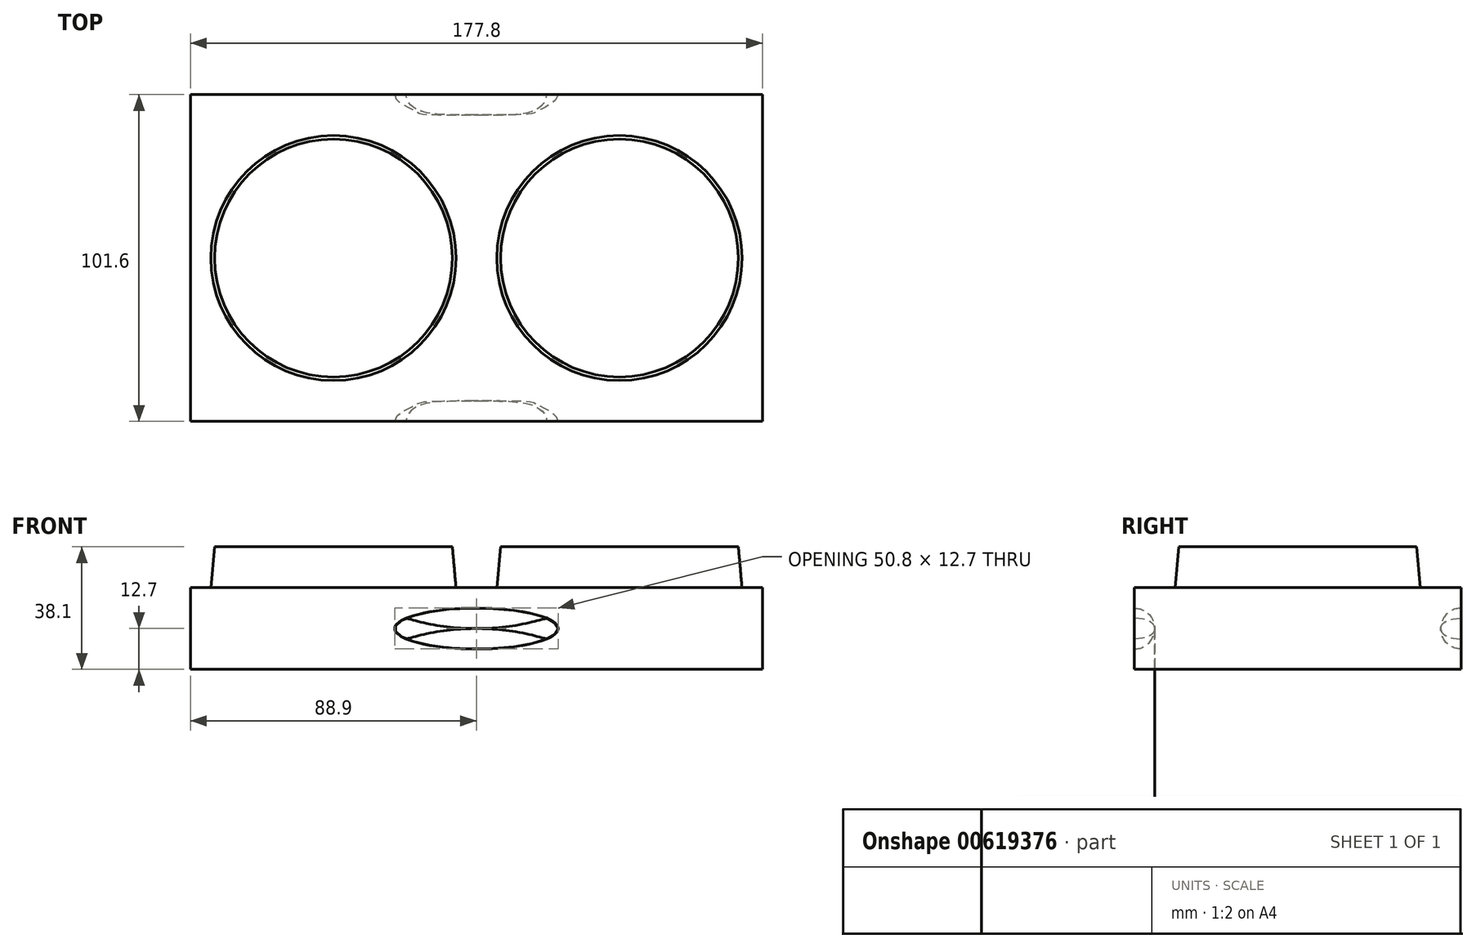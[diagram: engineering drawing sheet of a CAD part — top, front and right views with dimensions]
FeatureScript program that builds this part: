
annotation { "Feature Type Name" : "Feature", "Feature Type Description" : "" }
export const myFeature = defineFeature(function(context is Context, id is Id, definition is map)
    precondition{}
    {
        {
            var Q0;
            Q0=qCreatedBy(makeId("Top.planeOp"),FACE);
            var sketch = newSketch(context, id + "F0", { "sketchPlane" : qUnion([Q0])});
            skLineSegment(sketch, "E0.bottom", {"start": v(-88.9, 50.8) * mm, "end": v(88.9, 50.8) * mm});
            skLineSegment(sketch, "E0.top", {"start": v(-88.9, -50.8) * mm, "end": v(88.9, -50.8) * mm});
            skLineSegment(sketch, "E0.left", {"start": v(-88.9, 50.8) * mm, "end": v(-88.9, -50.8) * mm});
            skLineSegment(sketch, "E0.right", {"start": v(88.9, 50.8) * mm, "end": v(88.9, -50.8) * mm});
            skSolve(sketch);
        }
        {
            var Q0;
            Q0 = qSketchRegion(id + "F0", true);
            extrude(context, id + "F1", {"entities" : qUnion([Q0]), "depth" : 25.4 * mm, "offsetDistance" : 25.4 * mm});
        }
        {
            var Q0;
            Q0=makeQuery(id+"F1.opExtrude","CAP_FACE",FACE,{"disambiguationData":[OSD([sQuery(id+"F0.wireOp",EDGE,"E0.bottom"),sQuery(id+"F0.wireOp",EDGE,"E0.top"),sQuery(id+"F0.wireOp",EDGE,"E0.left"),sQuery(id+"F0.wireOp",EDGE,"E0.right")])],"isStart":false});
            var sketch = newSketch(context, id + "F2", { "sketchPlane" : qUnion([Q0])});
            skCircle(sketch, "E1", {"center": v(-44.45, 0) * mm, "radius": 38.09 * mm});
            skCircle(sketch, "E2", {"center": v(44.45, 0) * mm, "radius": 38.09 * mm});
            skSolve(sketch);
        }
        {
            var Q0;
            Q0 = qSketchRegion(id + "F2", true);
            extrude(context, id + "F3", {"entities" : qUnion([Q0]), "operationType" : NewBodyOperationType.ADD, "depth" : 12.7 * mm, "offsetDistance" : 25.4 * mm, "hasDraft" : true, "draftAngle" : 5 * degree, "draftPullDirection" : true});
        }
        {
            var Q0;
            Q0=makeQuery(id+"F1.opExtrude","SWEPT_FACE",FACE,{"disambiguationData":[OSD([sQuery(id+"F0.wireOp",EDGE,"E0.top")])]});
            var sketch = newSketch(context, id + "F4", { "sketchPlane" : qUnion([Q0])});
            skEllipse(sketch, "E3", {"center": v(0, 12.7) * mm, "majorRadius": 25.4 * mm, "minorRadius": 6.35 * mm, "majorAxis": v(1, 0)});
            skSolve(sketch);
        }
        {
            var Q0;
            Q0 = qSketchRegion(id + "F4", true);
            extrude(context, id + "F5", {"entities" : qUnion([Q0]), "operationType" : NewBodyOperationType.REMOVE, "oppositeDirection" : true, "depth" : 6.35 * mm, "offsetDistance" : 25.4 * mm});
        }
        {
            var Q0;
            Q0=makeQuery(id+"F5.boolean.opBoolean","COPY",EDGE,{"derivedFrom":makeQuery(id+"F5.opExtrude","CAP_EDGE",EDGE,{"disambiguationData":[OSD([sQuery(id+"F4.wireOp",EDGE,"E3")])],"isStart":false})});
            fillet(context, id + "F6", {"entities" : qUnion([Q0]), "radius" : 6.35 * mm, "tangentPropagation" : true, "allowEdgeOverflow" : false});
        }
        {
            var Q0;
            Q0=makeQuery(id+"F1.opExtrude","SWEPT_FACE",FACE,{"disambiguationData":[OSD([sQuery(id+"F0.wireOp",EDGE,"E0.bottom")])]});
            var sketch = newSketch(context, id + "F7", { "sketchPlane" : qUnion([Q0])});
            skEllipse(sketch, "E4", {"center": v(0, 12.7) * mm, "majorRadius": 25.4 * mm, "minorRadius": 6.35 * mm, "majorAxis": v(1, 0)});
            skSolve(sketch);
        }
        {
            var Q0;
            Q0 = qSketchRegion(id + "F7", true);
            extrude(context, id + "F8", {"entities" : qUnion([Q0]), "operationType" : NewBodyOperationType.REMOVE, "oppositeDirection" : true, "depth" : 6.35 * mm, "offsetDistance" : 25.4 * mm});
        }
        {
            var Q0;
            Q0=makeQuery(id+"F8.boolean.opBoolean","COPY",EDGE,{"derivedFrom":makeQuery(id+"F8.opExtrude","CAP_EDGE",EDGE,{"disambiguationData":[OSD([sQuery(id+"F7.wireOp",EDGE,"E4")])],"isStart":false})});
            fillet(context, id + "F9", {"entities" : qUnion([Q0]), "radius" : 6.35 * mm, "tangentPropagation" : true, "allowEdgeOverflow" : false});
        }
    });
